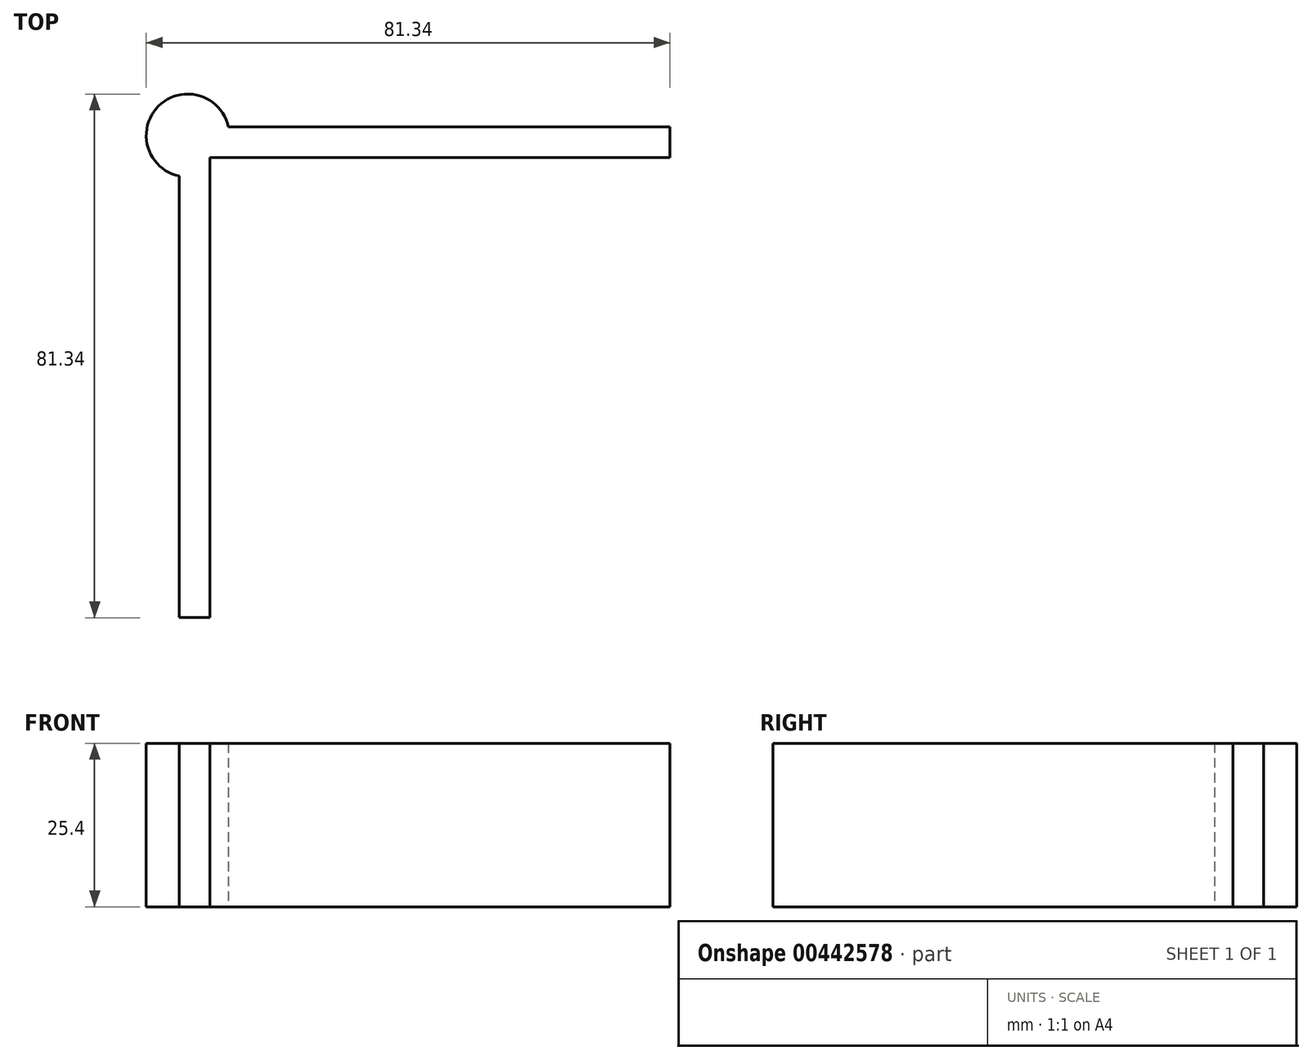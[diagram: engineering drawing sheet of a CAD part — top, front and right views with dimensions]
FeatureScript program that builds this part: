
annotation { "Feature Type Name" : "Feature", "Feature Type Description" : "" }
export const myFeature = defineFeature(function(context is Context, id is Id, definition is map)
    precondition{}
    {
        {
            var Q0;
            Q0=qCreatedBy(makeId("Top.planeOp"),FACE);
            var sketch = newSketch(context, id + "F0", { "sketchPlane" : qUnion([Q0])});
            skLineSegment(sketch, "E0.bottom", {"start": v(-39.62, 49.13) * mm, "end": v(36.58, 49.13) * mm});
            skLineSegment(sketch, "E0.left", {"start": v(-39.62, 49.13) * mm, "end": v(-39.62, -27.07) * mm});
            skLineSegment(sketch, "E1.bottom", {"start": v(-34.86, 44.37) * mm, "end": v(36.58, 44.37) * mm});
            skLineSegment(sketch, "E1.left", {"start": v(-34.86, 44.37) * mm, "end": v(-34.86, -27.07) * mm});
            skPoint(sketch, "E2", {"position": v(-39.62, 41.51) * mm});
            skPoint(sketch, "E3", {"position": v(-32, 49.13) * mm});
            skArc(sketch, "E4", {"start": v(-32, 49.13) * mm, "mid": v(-42.87, 52.38) * mm, "end": v(-39.62, 41.51) * mm});
            skLineSegment(sketch, "E5", {"start": v(-39.62, -27.07) * mm, "end": v(-34.86, -27.07) * mm});
            skLineSegment(sketch, "E6", {"start": v(36.58, 49.13) * mm, "end": v(36.58, 44.37) * mm});
            skSolve(sketch);
        }
        {
            var Q0;
            Q0=makeQuery(id+"F0.imprint","IMPRINT",FACE,{"disambiguationData":[TD([[makeQuery(id+"F0.imprint","IMPRINT",EDGE,{"derivedFrom":sQuery(id+"F0.wireOp",EDGE,"62dd1c21-4ef7-4e4a-8728-3a54cd1c0359.bottom")}),1.0]])]});
            var Q1;
            {var subQ3=sQuery(id+"F0.wireOp",EDGE,"10984230-8f1f-4229-89c1-024c3b5ad161");Q1=makeQuery(id+"F0.imprint","IMPRINT",FACE,{"disambiguationData":[TD([[makeQuery(id+"F0.imprint","IMPRINT",EDGE,{"derivedFrom":subQ3}),1.0]])]});}
            var Q2;
            Q2=makeQuery(id+"F0.imprint","IMPRINT",FACE,{"disambiguationData":[TD([[makeQuery(id+"F0.imprint","IMPRINT",EDGE,{"derivedFrom":sQuery(id+"F0.wireOp",EDGE,"36f35aef-9c42-4bd3-83f7-382151b07b01.bottom")}),1.0]])]});
            var Q3;
            {var subQ3=sQuery(id+"F0.wireOp",EDGE,"7c4ab9aa-769f-424e-97bb-2b17f0463f34");Q3=makeQuery(id+"F0.imprint","IMPRINT",FACE,{"disambiguationData":[TD([[makeQuery(id+"F0.imprint","IMPRINT",EDGE,{"derivedFrom":subQ3}),1.0]])]});}
            var Q4;
            Q4=makeQuery(id+"F0.imprint","IMPRINT",FACE,{"disambiguationData":[TD([[makeQuery(id+"F0.imprint","IMPRINT",EDGE,{"derivedFrom":sQuery(id+"F0.wireOp",EDGE,"7c03809b-e613-4294-a1c0-451a204511b9.bottom")}),1.0]])]});
            var Q5;
            {var subQ3=sQuery(id+"F0.wireOp",EDGE,"4e3b6fe9-e600-44c0-97dd-b27f0f09a795");Q5=makeQuery(id+"F0.imprint","IMPRINT",FACE,{"disambiguationData":[TD([[makeQuery(id+"F0.imprint","IMPRINT",EDGE,{"derivedFrom":subQ3}),1.0]])]});}
            var Q6;
            Q6=makeQuery(id+"F0.imprint","IMPRINT",FACE,{"disambiguationData":[TD([[makeQuery(id+"F0.imprint","IMPRINT",EDGE,{"derivedFrom":sQuery(id+"F0.wireOp",EDGE,"abecbff8-e1e5-40c8-a0f5-1bf2474d33cd.bottom")}),1.0]])]});
            var Q7;
            {var subQ3=sQuery(id+"F0.wireOp",EDGE,"4ede7a5c-e325-494f-9b2d-ee84c5afdbcc");Q7=makeQuery(id+"F0.imprint","IMPRINT",FACE,{"disambiguationData":[TD([[makeQuery(id+"F0.imprint","IMPRINT",EDGE,{"derivedFrom":subQ3}),1.0]])]});}
            var Q8;
            Q8=makeQuery(id+"F0.imprint","IMPRINT",FACE,{"disambiguationData":[TD([[makeQuery(id+"F0.imprint","IMPRINT",EDGE,{"derivedFrom":sQuery(id+"F0.wireOp",EDGE,"b02efde2-2e34-48bb-b0c9-166184739106.bottom")}),1.0]])]});
            var Q9;
            {var subQ3=sQuery(id+"F0.wireOp",EDGE,"b057d806-97a8-4b87-823d-fdd6fe6935e5");Q9=makeQuery(id+"F0.imprint","IMPRINT",FACE,{"disambiguationData":[TD([[makeQuery(id+"F0.imprint","IMPRINT",EDGE,{"derivedFrom":subQ3}),1.0]])]});}
            var Q10;
            Q10=makeQuery(id+"F0.imprint","IMPRINT",FACE,{"disambiguationData":[TD([[makeQuery(id+"F0.imprint","IMPRINT",EDGE,{"derivedFrom":sQuery(id+"F0.wireOp",EDGE,"d79e77e3-9958-43a9-89b4-ffaff2acf329.bottom")}),1.0]])]});
            var Q11;
            {var subQ3=sQuery(id+"F0.wireOp",EDGE,"42c3b786-203a-48b7-aac5-35461c9db278");Q11=makeQuery(id+"F0.imprint","IMPRINT",FACE,{"disambiguationData":[TD([[makeQuery(id+"F0.imprint","IMPRINT",EDGE,{"derivedFrom":subQ3}),1.0]])]});}
            var Q12;
            {var subQ3=sQuery(id+"F0.wireOp",EDGE,"01312014-4ec8-42a1-b136-f639ef1237ea");Q12=makeQuery(id+"F0.imprint","IMPRINT",FACE,{"disambiguationData":[TD([[makeQuery(id+"F0.imprint","IMPRINT",EDGE,{"derivedFrom":subQ3}),1.0]])]});}
            var Q13;
            Q13=makeQuery(id+"F0.imprint","IMPRINT",FACE,{"disambiguationData":[TD([[makeQuery(id+"F0.imprint","IMPRINT",EDGE,{"derivedFrom":sQuery(id+"F0.wireOp",EDGE,"08e5f1c8-7457-4b17-ae78-5c34079a4098.bottom")}),1.0]])]});
            var Q14;
            Q14=makeQuery(id+"F0.imprint","IMPRINT",FACE,{"disambiguationData":[TD([[makeQuery(id+"F0.imprint","IMPRINT",EDGE,{"derivedFrom":sQuery(id+"F0.wireOp",EDGE,"2c0adb98-abda-460c-b48c-32c3437da891.bottom")}),1.0]])]});
            var Q15;
            {var subQ3=sQuery(id+"F0.wireOp",EDGE,"0a3f9932-ad4e-4c30-8cf6-87b0545028eb");Q15=makeQuery(id+"F0.imprint","IMPRINT",FACE,{"disambiguationData":[TD([[makeQuery(id+"F0.imprint","IMPRINT",EDGE,{"derivedFrom":subQ3}),1.0]])]});}
            var Q16;
            Q16=makeQuery(id+"F0.imprint","IMPRINT",FACE,{"disambiguationData":[TD([[makeQuery(id+"F0.imprint","IMPRINT",EDGE,{"derivedFrom":sQuery(id+"F0.wireOp",EDGE,"9cadbe4e-89ab-49dc-a32c-cb5cfd5667c7.bottom")}),1.0]])]});
            var Q17;
            {var subQ3=sQuery(id+"F0.wireOp",EDGE,"18c18f0d-2c02-4828-a906-09c190f209f2");Q17=makeQuery(id+"F0.imprint","IMPRINT",FACE,{"disambiguationData":[TD([[makeQuery(id+"F0.imprint","IMPRINT",EDGE,{"derivedFrom":subQ3}),1.0]])]});}
            var Q18;
            Q18=makeQuery(id+"F0.imprint","IMPRINT",FACE,{"disambiguationData":[TD([[makeQuery(id+"F0.imprint","IMPRINT",EDGE,{"derivedFrom":sQuery(id+"F0.wireOp",EDGE,"E1.bottom")}),1.0]])]});
            var Q19;
            {var subQ3=sQuery(id+"F0.wireOp",EDGE,"E4");Q19=makeQuery(id+"F0.imprint","IMPRINT",FACE,{"disambiguationData":[TD([[makeQuery(id+"F0.imprint","IMPRINT",EDGE,{"derivedFrom":subQ3}),1.0]])]});}
            extrude(context, id + "F1", {"entities" : qUnion([Q0, Q1, Q2, Q3, Q4, Q5, Q6, Q7, Q8, Q9, Q10, Q11, Q12, Q13, Q14, Q15, Q16, Q17, Q18, Q19]), "depth" : 25.4 * mm});
        }
    });
